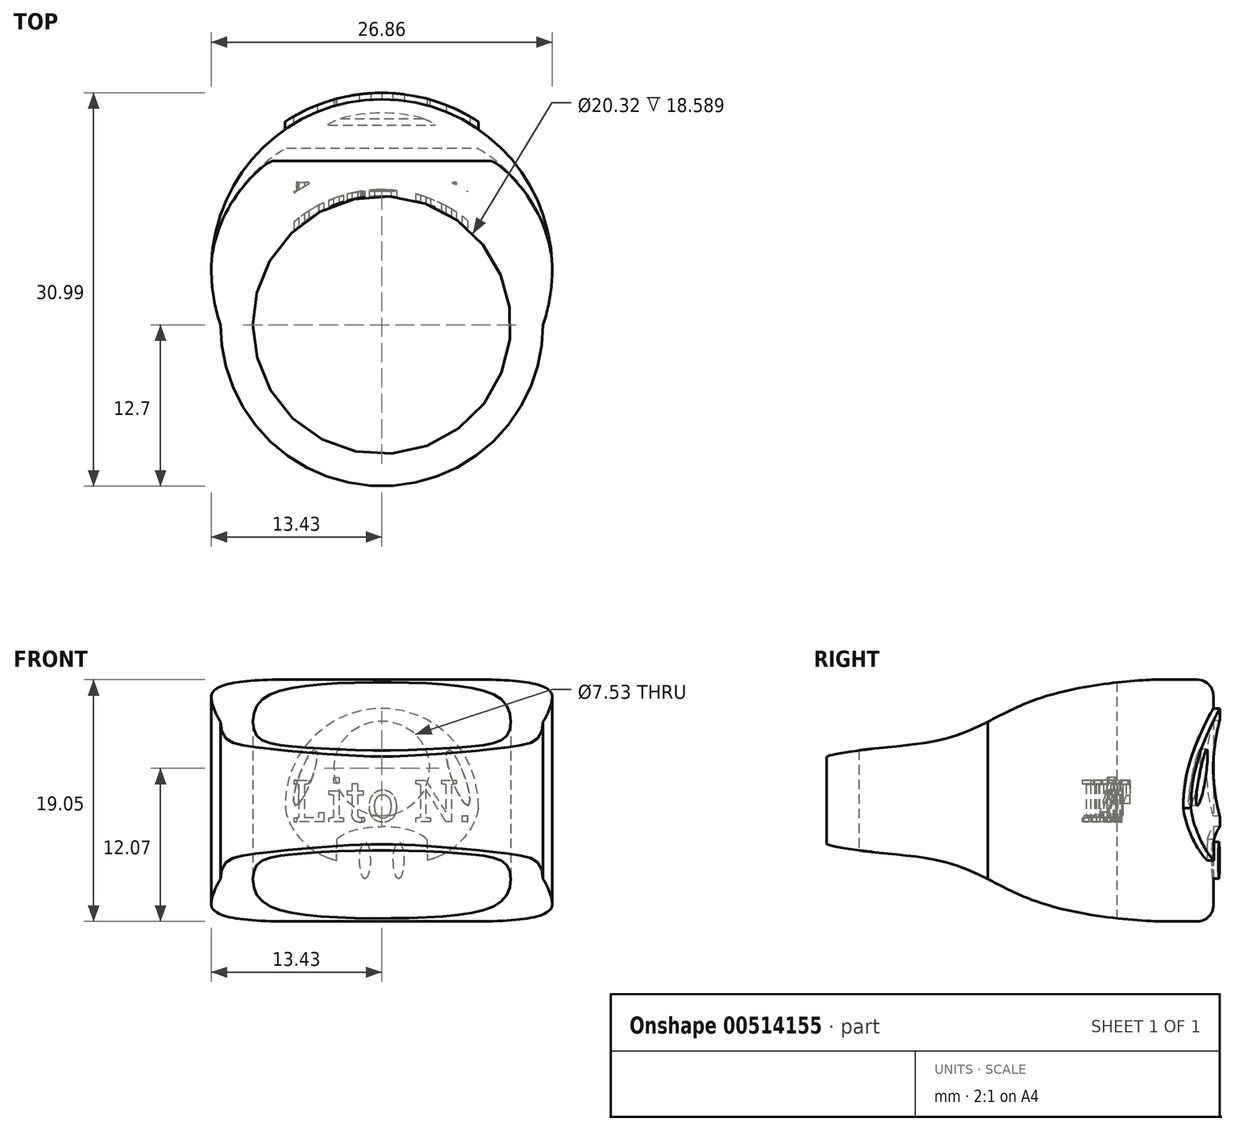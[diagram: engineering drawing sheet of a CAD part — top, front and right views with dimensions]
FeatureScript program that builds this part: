
annotation { "Feature Type Name" : "Feature", "Feature Type Description" : "" }
export const myFeature = defineFeature(function(context is Context, id is Id, definition is map)
    precondition{}
    {
        {
            var Q0;
            Q0=qCreatedBy(makeId("Top.planeOp"),FACE);
            var sketch = newSketch(context, id + "F0", { "sketchPlane" : qUnion([Q0])});
            skCircle(sketch, "E0", {"center": v(0, 0) * mm, "radius": 10.16 * mm});
            skArc(sketch, "E1", {"start": v(-12.7, 0) * mm, "mid": v(0, -12.7) * mm, "end": v(12.7, 0) * mm});
            skArc(sketch, "E2", {"start": v(12.7, 0) * mm, "mid": v(0, 17.78) * mm, "end": v(-12.7, 0) * mm});
            skSolve(sketch);
        }
        {
            var Q0;
            Q0=makeQuery(id+"F0.imprint","IMPRINT",FACE,{"disambiguationData":[TD([[makeQuery(id+"F0.imprint","IMPRINT",EDGE,{"derivedFrom":sQuery(id+"F0.wireOp",EDGE,"E0")}),-1.0]])]});
            extrude(context, id + "F1", {"entities" : qUnion([Q0]), "depth" : 19.05 * mm});
        }
        {
            var Q0;
            Q0=qCreatedBy(makeId("Front.planeOp"),FACE);
            var sketch = newSketch(context, id + "F2", { "sketchPlane" : qUnion([Q0])});
            skText(sketch, "E3", { "text": "Lito N.", "fontName": "RobotoSlab-Regular.ttf"});
            const initialGuessF2  = {"E3": [-0.00707, 0.00787, 1, 0, 0.0033]};
            skSetInitialGuess(sketch, initialGuessF2);
            skSolve(sketch);
        }
        {
            var Q0;
            Q0=qSketchRegion(id+"F2",true);
            var Q1;
            Q1=qConstructionFilter(qBodyType(qCreatedBy(id+"F2",EDGE),BodyType.WIRE),ConstructionObject.NO);
            extrude(context, id + "F3", {"entities" : qUnion([Q0]), "operationType" : NewBodyOperationType.REMOVE, "surfaceEntities" : qUnion([Q1]), "oppositeDirection" : true, "depth" : 11.23 * mm, "hasSecondDirection" : true, "secondDirectionOppositeDirection" : true, "secondDirectionDepth" : 7.24 * mm});
        }
        {
            var Q0;
            Q0=qCreatedBy(makeId("Top.planeOp"),FACE);
            var sketch = newSketch(context, id + "F4", { "sketchPlane" : qUnion([Q0])});
            skCircle(sketch, "E4", {"center": v(0, 0) * mm, "radius": 10.66 * mm});
            skCircle(sketch, "E5", {"center": v(0, 0) * mm, "radius": 12.5 * mm});
            skSolve(sketch);
        }
        {
            var Q0;
            Q0=makeQuery(id+"F4.imprint","IMPRINT",FACE,{"disambiguationData":[TD([[makeQuery(id+"F4.imprint","IMPRINT",EDGE,{"derivedFrom":sQuery(id+"F4.wireOp",EDGE,"E4")}),-1.0]])]});
            extrude(context, id + "F5", {"entities" : qUnion([Q0]), "operationType" : NewBodyOperationType.ADD, "depth" : 19.05 * mm});
        }
        {
            var Q0;
            Q0=makeQuery(id+"F1.opExtrude","CAP_EDGE",EDGE,{"disambiguationData":[OSD([sQuery(id+"F0.wireOp",EDGE,"E2")])],"isStart":false});
            var Q1;
            Q1=makeQuery(id+"F1.opExtrude","CAP_EDGE",EDGE,{"disambiguationData":[OSD([sQuery(id+"F0.wireOp",EDGE,"E2")])],"isStart":true});
            fillet(context, id + "F6", {"entities" : qUnion([Q0, Q1]), "radius" : 1.27 * mm, "tangentPropagation" : true, "allowEdgeOverflow" : false});
        }
        {
            var Q0;
            Q0=qCreatedBy(makeId("Right.planeOp"),FACE);
            var sketch = newSketch(context, id + "F7", { "sketchPlane" : qUnion([Q0])});
            skLineSegment(sketch, "E6", {"start": v(29.01, 9.54) * mm, "end": v(-18.1, 9.54) * mm});
            skFitSpline(sketch, "E7", {"points": [v(16.27, 19.07) * mm, v(3.6, 17.42) * mm, v(-3.17, 14.45) * mm, v(-12.74, 13) * mm], "startDerivative": vector(-34.03, 1.2) * mm, "endDerivative": vector(-25.58, -7.08) * mm});
            skLineSegment(sketch, "E8", {"start": v(16.27, 19.07) * mm, "end": v(19.29, 19.07) * mm});
            skLineSegment(sketch, "E9", {"start": v(19.29, 19.07) * mm, "end": v(19.29, 9.54) * mm});
            skLineSegment(sketch, "E10", {"start": v(-12.74, 13) * mm, "end": v(-12.8, 13) * mm});
            skLineSegment(sketch, "E11", {"start": v(-12.8, 13) * mm, "end": v(-12.8, 9.54) * mm});
            skLineSegment(sketch, "E12", {"start": v(21.42, 9.54) * mm, "end": v(21.42, 22.8) * mm});
            skLineSegment(sketch, "E13", {"start": v(21.42, 22.8) * mm, "end": v(-16.06, 22.8) * mm});
            skLineSegment(sketch, "E14", {"start": v(-16.06, 22.8) * mm, "end": v(-16.06, 9.54) * mm});
            skFitSpline(sketch, "E15.MirrorCS", {"points": [v(16.27, 0.01) * mm, v(3.6, 1.66) * mm, v(-3.17, 4.64) * mm, v(-12.74, 6.09) * mm], "startDerivative": vector(-34.03, -1.2) * mm, "endDerivative": vector(-25.58, 7.08) * mm});
            skLineSegment(sketch, "E16.MirrorCS", {"start": v(16.27, 0.01) * mm, "end": v(19.29, 0.01) * mm});
            skLineSegment(sketch, "E17.MirrorCS", {"start": v(19.29, 0.01) * mm, "end": v(19.29, 9.54) * mm});
            skLineSegment(sketch, "E18.MirrorCS", {"start": v(21.42, -3.71) * mm, "end": v(-16.06, -3.71) * mm});
            skLineSegment(sketch, "E19.MirrorCS", {"start": v(21.42, 9.54) * mm, "end": v(21.42, -3.71) * mm});
            skLineSegment(sketch, "E20.MirrorCS", {"start": v(-16.06, -3.71) * mm, "end": v(-16.06, 9.54) * mm});
            skLineSegment(sketch, "E21.MirrorCS", {"start": v(-12.8, 6.09) * mm, "end": v(-12.8, 9.54) * mm});
            skLineSegment(sketch, "E22.MirrorCS", {"start": v(-12.74, 6.09) * mm, "end": v(-12.8, 6.09) * mm});
            skSolve(sketch);
        }
        {
            var Q0;
            Q0=makeQuery(id+"F7.imprint","IMPRINT",FACE,{"disambiguationData":[TD([[makeQuery(id+"F7.imprint","IMPRINT",EDGE,{"derivedFrom":sQuery(id+"F7.wireOp",EDGE,"E7")}),-1.0]])]});
            var Q1;
            Q1=makeQuery(id+"F7.imprint","IMPRINT",FACE,{"disambiguationData":[TD([[makeQuery(id+"F7.imprint","IMPRINT",EDGE,{"derivedFrom":sQuery(id+"F7.wireOp",EDGE,"E15.MirrorCS")}),1.0]])]});
            extrude(context, id + "F8", {"entities" : qUnion([Q0, Q1]), "operationType" : NewBodyOperationType.REMOVE, "oppositeDirection" : true, "depth" : 25.4 * mm, "hasSecondDirection" : true, "secondDirectionOppositeDirection" : false, "secondDirectionDepth" : 25.4 * mm});
        }
        {
            var Q0;
            Q0=qCreatedBy(makeId("Front.planeOp"),FACE);
            var sketch = newSketch(context, id + "F9", { "sketchPlane" : qUnion([Q0])});
            skLineSegment(sketch, "E23", {"start": v(0, 15.75) * mm, "end": v(0, -9.15) * mm, "construction": true});
            skLineSegment(sketch, "E24", {"start": v(0, 9.18) * mm, "end": v(0, 1.35) * mm});
            skArc(sketch, "E25", {"start": v(7.46, 7.68) * mm, "mid": v(-0.87, 16.73) * mm, "end": v(-6.93, 6.03) * mm});
            skFitSpline(sketch, "E26", {"points": [v(7.6, 8.94) * mm, v(5.1, 5.42) * mm, v(0, 4.6) * mm], "startDerivative": vector(-0.9, -7.9) * mm, "endDerivative": vector(-10.3, 0.68) * mm});
            skFitSpline(sketch, "E27.MirrorCS", {"points": [v(-7.6, 8.94) * mm, v(-5.1, 5.42) * mm, v(0, 4.6) * mm], "startDerivative": vector(0.9, -7.9) * mm, "endDerivative": vector(10.3, 0.68) * mm});
            skFitSpline(sketch, "E28", {"points": [v(4.26, 5.02) * mm, v(3.83, 3.1) * mm, v(2.12, 1.87) * mm, v(0, 1.57) * mm], "startDerivative": vector(-0.4, -6.07) * mm, "endDerivative": vector(-6.22, -0.29) * mm});
            skFitSpline(sketch, "E29.MirrorCS", {"points": [v(-4.26, 5.02) * mm, v(-3.83, 3.1) * mm, v(-2.12, 1.87) * mm, v(0, 1.57) * mm], "startDerivative": vector(0.4, -6.07) * mm, "endDerivative": vector(6.22, -0.29) * mm});
            skEllipse(sketch, "E30", {"center": v(-6.02, 11.34) * mm, "majorRadius": 2.35 * mm, "minorRadius": 0.5 * mm, "majorAxis": v(-0.34, -0.94)});
            skCircle(sketch, "E31", {"center": v(0, 12.07) * mm, "radius": 3.77 * mm});
            skEllipse(sketch, "E32.MirrorC", {"center": v(6.02, 11.34) * mm, "majorRadius": 2.35 * mm, "minorRadius": 0.5 * mm, "majorAxis": v(0.34, -0.94)});
            skFitSpline(sketch, "E33", {"points": [v(-3.55, 6.46) * mm, v(-3.32, 3.56) * mm, v(-1.97, 2.56) * mm, v(0, 2.27) * mm], "startDerivative": vector(-0.23, -6.3) * mm, "endDerivative": vector(6.52, -0.22) * mm});
            skEllipse(sketch, "E34", {"center": v(-1.32, 4.82) * mm, "majorRadius": 1.44 * mm, "minorRadius": 0.45 * mm, "majorAxis": v(0, -1)});
            skFitSpline(sketch, "E35", {"points": [v(-3.55, 6.46) * mm, v(-1.85, 7.28) * mm, v(0, 7.49) * mm], "startDerivative": vector(3.05, 2.76) * mm, "endDerivative": vector(4.06, 0.23) * mm});
            skFitSpline(sketch, "E36.MirrorCS", {"points": [v(3.55, 6.46) * mm, v(1.85, 7.28) * mm, v(0, 7.49) * mm], "startDerivative": vector(-3.05, 2.76) * mm, "endDerivative": vector(-4.06, 0.23) * mm});
            skFitSpline(sketch, "E37.MirrorCS", {"points": [v(3.55, 6.46) * mm, v(3.32, 3.56) * mm, v(1.97, 2.56) * mm, v(0, 2.27) * mm], "startDerivative": vector(0.23, -6.3) * mm, "endDerivative": vector(-6.52, -0.22) * mm});
            skEllipse(sketch, "E38.MirrorC", {"center": v(1.32, 4.82) * mm, "majorRadius": 1.44 * mm, "minorRadius": 0.45 * mm, "majorAxis": v(0, -1)});
            skSolve(sketch);
        }
        {
            var Q0;
            {var subQ0=sQuery(id+"F9.wireOp",EDGE,"HgEMAO3P-VkiK-e8zG-XvVL-0NStHSkwPYVQ");Q0=makeQuery(id+"F9.imprint","IMPRINT",FACE,{"disambiguationData":[TD([[makeQuery(id+"F9.imprint","IMPRINT",EDGE,{"derivedFrom":subQ0}),1.0]])]});}
            var Q1;
            Q1=makeQuery(id+"F9.imprint","IMPRINT",FACE,{"disambiguationData":[TD([[makeQuery(id+"F9.imprint","IMPRINT",EDGE,{"derivedFrom":sQuery(id+"F9.wireOp",EDGE,"E25")}),1.0]])]});
            var Q2;
            {var subQ0=sQuery(id+"F9.wireOp",EDGE,"c84a23ae-ecd5-441c-b0fd-af62929562ba.trimOffspring");Q2=makeQuery(id+"F9.imprint","IMPRINT",FACE,{"disambiguationData":[TD([[makeQuery(id+"F9.imprint","IMPRINT",EDGE,{"derivedFrom":subQ0}),1.0]])]});}
            var Q3;
            {var subQ0=sQuery(id+"F9.wireOp",EDGE,"757HnZQb-4AL5-fsaC-PdVJ-4zn3AztpkORW");Q3=makeQuery(id+"F9.imprint","IMPRINT",FACE,{"disambiguationData":[TD([[makeQuery(id+"F9.imprint","IMPRINT",EDGE,{"derivedFrom":subQ0}),1.0]])]});}
            var Q4;
            {var subQ5=sQuery(id+"F9.wireOp",EDGE,"VWwuiQ4b-7hVG-qatS-JJWG-rpj4fduQvBo1");Q4=makeQuery(id+"F9.imprint","IMPRINT",FACE,{"disambiguationData":[TD([[makeQuery(id+"F9.imprint","IMPRINT",EDGE,{"derivedFrom":subQ5}),1.0]])]});}
            var Q5;
            Q5=makeQuery(id+"F9.imprint","IMPRINT",FACE,{"disambiguationData":[TD([[makeQuery(id+"F9.imprint","IMPRINT",EDGE,{"derivedFrom":sQuery(id+"F9.wireOp",EDGE,"E38.MirrorC")}),1.0]])]});
            var Q6;
            Q6=makeQuery(id+"F9.imprint","IMPRINT",FACE,{"disambiguationData":[TD([[makeQuery(id+"F9.imprint","IMPRINT",EDGE,{"derivedFrom":sQuery(id+"F9.wireOp",EDGE,"E34")}),1.0]])]});
            extrude(context, id + "F10", {"entities" : qUnion([Q0, Q1, Q2, Q3, Q4, Q5, Q6]), "operationType" : NewBodyOperationType.ADD, "oppositeDirection" : true, "depth" : 20.32 * mm, "hasSecondDirection" : true, "secondDirectionOppositeDirection" : true, "secondDirectionDepth" : 10.54 * mm, "offsetDistance" : 25.4 * mm});
        }
        {
            var Q0;
            Q0=qCreatedBy(makeId("Top.planeOp"),FACE);
            var sketch = newSketch(context, id + "F11", { "sketchPlane" : qUnion([Q0])});
            skArc(sketch, "E39", {"start": v(13.2, 0) * mm, "mid": v(0, 18.29) * mm, "end": v(-13.2, 0) * mm});
            skLineSegment(sketch, "E40", {"start": v(13.2, 0) * mm, "end": v(15.4, 0) * mm});
            skLineSegment(sketch, "E41", {"start": v(15.4, 0) * mm, "end": v(15.4, 21.9) * mm});
            skLineSegment(sketch, "E42", {"start": v(15.4, 21.9) * mm, "end": v(-16.46, 21.9) * mm});
            skLineSegment(sketch, "E43", {"start": v(-16.46, 21.9) * mm, "end": v(-16.46, 0) * mm});
            skLineSegment(sketch, "E44", {"start": v(-16.46, 0) * mm, "end": v(-13.2, 0) * mm});
            skSolve(sketch);
        }
        {
            var Q0;
            Q0=makeQuery(id+"F11.imprint","IMPRINT",FACE,{"disambiguationData":[TD([[makeQuery(id+"F11.imprint","IMPRINT",EDGE,{"derivedFrom":sQuery(id+"F11.wireOp",EDGE,"E39")}),-1.0]])]});
            extrude(context, id + "F12", {"entities" : qUnion([Q0]), "operationType" : NewBodyOperationType.REMOVE, "depth" : 25.4 * mm});
        }
    });
